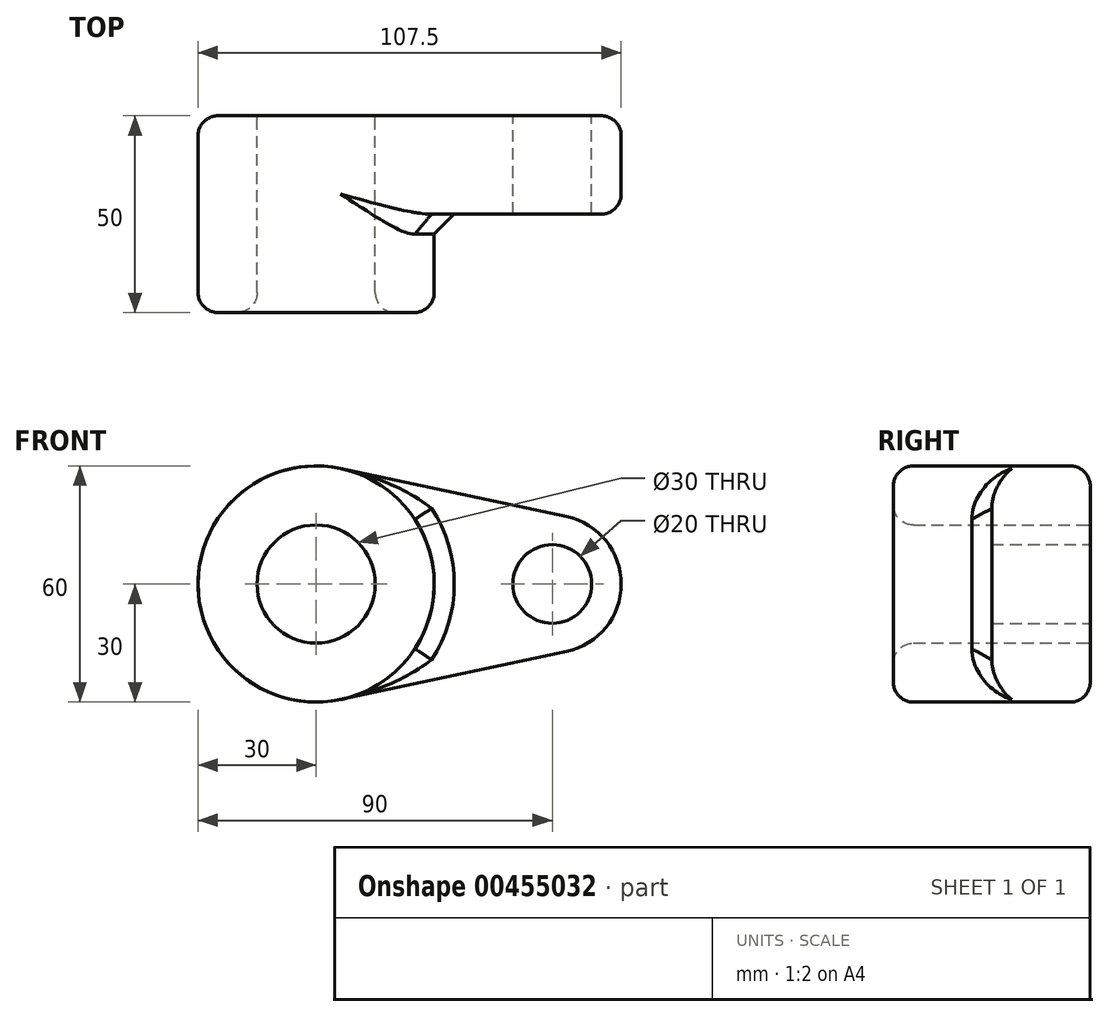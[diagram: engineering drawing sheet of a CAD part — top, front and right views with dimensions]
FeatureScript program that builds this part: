
annotation { "Feature Type Name" : "Feature", "Feature Type Description" : "" }
export const myFeature = defineFeature(function(context is Context, id is Id, definition is map)
    precondition{}
    {
        {
            var Q0;
            Q0=qCreatedBy(makeId("Front.planeOp"),FACE);
            var sketch = newSketch(context, id + "F0", { "sketchPlane" : qUnion([Q0])});
            skCircle(sketch, "E0", {"center": v(0, 0) * mm, "radius": 30 * mm});
            skCircle(sketch, "E1", {"center": v(60, 0) * mm, "radius": 17.5 * mm});
            skLineSegment(sketch, "E2", {"start": v(6.25, 29.34) * mm, "end": v(63.65, 17.12) * mm});
            skLineSegment(sketch, "E3", {"start": v(6.25, -29.34) * mm, "end": v(63.65, -17.12) * mm});
            skCircle(sketch, "E4", {"center": v(60, 0) * mm, "radius": 10 * mm});
            skCircle(sketch, "E5", {"center": v(0, 0) * mm, "radius": 15 * mm});
            skSolve(sketch);
        }
        {
            var Q0;
            Q0 = qSketchRegion(id + "F0", true);
            extrude(context, id + "F1", {"entities" : qUnion([Q0]), "depth" : 25 * mm});
        }
        {
            var Q0;
            Q0=makeQuery(id+"F0.imprint","IMPRINT",FACE,{"disambiguationData":[TD([[makeQuery(id+"F0.imprint","IMPRINT",EDGE,{"derivedFrom":sQuery(id+"F0.wireOp",EDGE,"E5")}),-1.0]])]});
            extrude(context, id + "F2", {"entities" : qUnion([Q0]), "operationType" : NewBodyOperationType.ADD, "depth" : 50 * mm});
        }
        {
            var Q0;
            Q0=makeQuery(id+"F2.opExtrude","CAP_FACE",FACE,{"disambiguationData":[OSD([sQuery(id+"F0.wireOp",EDGE,"E0"),sQuery(id+"F0.wireOp",EDGE,"E5")])],"isStart":false});
            var Q1;
            Q1=makeQuery(id+"F1.opExtrude","SWEPT_FACE",FACE,{"disambiguationData":[OSD([sQuery(id+"F0.wireOp",EDGE,"E3")])]});
            fillet(context, id + "F3", {"entities" : qUnion([Q0, Q1]), "radius" : 5.08 * mm, "tangentPropagation" : true, "allowEdgeOverflow" : false});
        }
        {
            var Q0;
            {var subQ0=sQuery(id+"F0.wireOp",EDGE,"E0");Q0=makeQuery(id+"F2.boolean.opBoolean","INTERSECT",EDGE,{"derivedFrom":[makeQuery(id+"F1.opExtrude","CAP_FACE",FACE,{"disambiguationData":[OSD([subQ0,sQuery(id+"F0.wireOp",EDGE,"E1"),sQuery(id+"F0.wireOp",EDGE,"E2"),sQuery(id+"F0.wireOp",EDGE,"E3"),sQuery(id+"F0.wireOp",EDGE,"E4"),sQuery(id+"F0.wireOp",EDGE,"E5")])],"isStart":false}),makeQuery(id+"F2.opExtrude","SWEPT_FACE",FACE,{"disambiguationData":[OSD([subQ0])]})]});}
            var Q1;
            {var subQ0=sQuery(id+"F0.wireOp",EDGE,"E0");Q1=makeQuery(id+"F2.boolean.opBoolean","MERGE",FACE,{"derivedFrom":[makeQuery(id+"F1.opExtrude","SWEPT_FACE",FACE,{"disambiguationData":[OSD([subQ0])]}),makeQuery(id+"F2.opExtrude","SWEPT_FACE",FACE,{"disambiguationData":[OSD([subQ0])]})]});}
            chamfer(context, id + "F4", {"entities" : qUnion([Q0, Q1]), "width" : 5.08 * mm, "tangentPropagation" : true});
        }
    });
